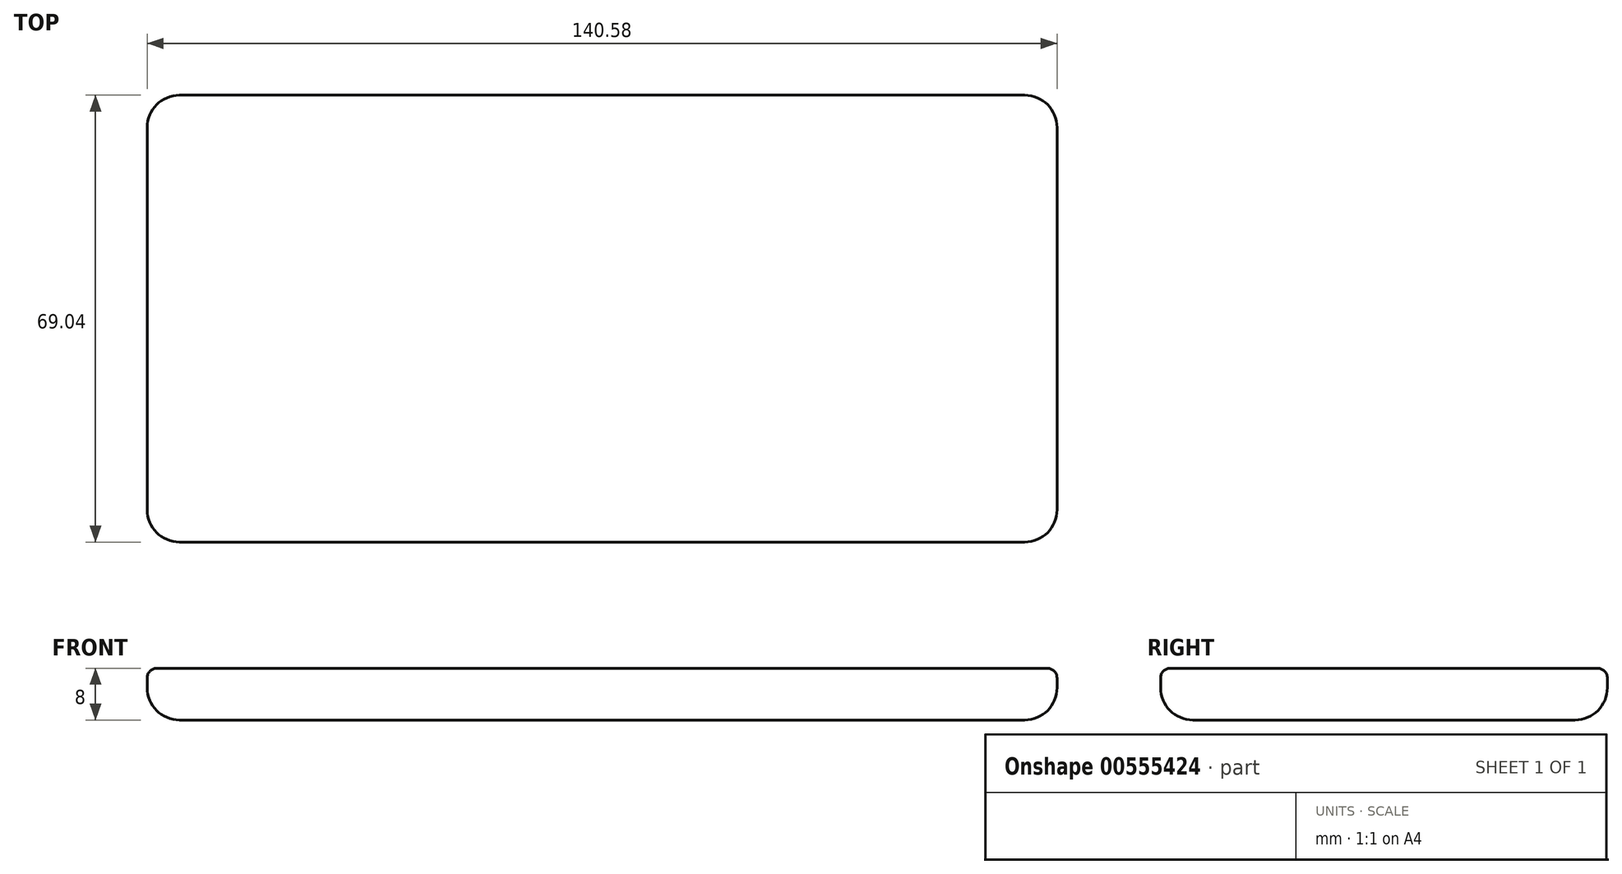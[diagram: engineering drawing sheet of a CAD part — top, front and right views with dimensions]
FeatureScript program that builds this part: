
annotation { "Feature Type Name" : "Feature", "Feature Type Description" : "" }
export const myFeature = defineFeature(function(context is Context, id is Id, definition is map)
    precondition{}
    {
        {
            var Q0;
            Q0=qCreatedBy(makeId("Top.planeOp"),FACE);
            var sketch = newSketch(context, id + "F0", { "sketchPlane" : qUnion([Q0])});
            skLineSegment(sketch, "E0.bottom", {"start": v(-65.3, 34.52) * mm, "end": v(65.3, 34.52) * mm});
            skLineSegment(sketch, "E0.top", {"start": v(-65.3, -34.52) * mm, "end": v(65.3, -34.52) * mm});
            skLineSegment(sketch, "E0.left", {"start": v(-70.3, 29.52) * mm, "end": v(-70.3, -29.52) * mm});
            skLineSegment(sketch, "E0.right", {"start": v(70.3, 29.52) * mm, "end": v(70.3, -29.52) * mm});
            skPoint(sketch, "E0.middle", {"position": v(0, 0) * mm});
            skPoint(sketch, "E1.visualSharp", {"position": v(-70.3, -34.52) * mm});
            skArc(sketch, "E1.filletArc", {"start": v(-70.3, -29.52) * mm, "mid": v(-68.83, -33.06) * mm, "end": v(-65.3, -34.52) * mm});
            skPoint(sketch, "E2.visualSharp", {"position": v(-70.3, 34.52) * mm});
            skArc(sketch, "E2.filletArc", {"start": v(-65.3, 34.52) * mm, "mid": v(-68.83, 33.06) * mm, "end": v(-70.3, 29.52) * mm});
            skPoint(sketch, "E3.visualSharp", {"position": v(70.3, 34.52) * mm});
            skArc(sketch, "E3.filletArc", {"start": v(70.3, 29.52) * mm, "mid": v(68.83, 33.06) * mm, "end": v(65.3, 34.52) * mm});
            skPoint(sketch, "E4.visualSharp", {"position": v(70.3, -34.52) * mm});
            skArc(sketch, "E4.filletArc", {"start": v(65.3, -34.52) * mm, "mid": v(68.83, -33.06) * mm, "end": v(70.3, -29.52) * mm});
            skSolve(sketch);
        }
        {
            var Q0;
            Q0=makeQuery(id+"F0.imprint","IMPRINT",FACE,{"disambiguationData":[TD([[makeQuery(id+"F0.imprint","IMPRINT",EDGE,{"derivedFrom":sQuery(id+"F0.wireOp",EDGE,"E0.bottom")}),-1.0]])]});
            extrude(context, id + "F1", {"entities" : qUnion([Q0]), "depth" : 8 * mm, "offsetDistance" : 25 * mm});
        }
        {
            var Q0;
            Q0=makeQuery(id+"F1.opExtrude","CAP_FACE",FACE,{"disambiguationData":[OSD([sQuery(id+"F0.wireOp",EDGE,"E0.bottom"),sQuery(id+"F0.wireOp",EDGE,"E0.top"),sQuery(id+"F0.wireOp",EDGE,"E0.left"),sQuery(id+"F0.wireOp",EDGE,"E0.right"),sQuery(id+"F0.wireOp",EDGE,"E1.filletArc"),sQuery(id+"F0.wireOp",EDGE,"E2.filletArc"),sQuery(id+"F0.wireOp",EDGE,"E3.filletArc"),sQuery(id+"F0.wireOp",EDGE,"E4.filletArc")])],"isStart":false});
            fillet(context, id + "F2", {"entities" : qUnion([Q0]), "radius" : 1.5 * mm, "tangentPropagation" : true, "allowEdgeOverflow" : false});
        }
        {
            var Q0;
            Q0=makeQuery(id+"F1.opExtrude","CAP_FACE",FACE,{"disambiguationData":[OSD([sQuery(id+"F0.wireOp",EDGE,"E0.bottom"),sQuery(id+"F0.wireOp",EDGE,"E0.top"),sQuery(id+"F0.wireOp",EDGE,"E0.left"),sQuery(id+"F0.wireOp",EDGE,"E0.right"),sQuery(id+"F0.wireOp",EDGE,"E1.filletArc"),sQuery(id+"F0.wireOp",EDGE,"E2.filletArc"),sQuery(id+"F0.wireOp",EDGE,"E3.filletArc"),sQuery(id+"F0.wireOp",EDGE,"E4.filletArc")])],"isStart":true});
            fillet(context, id + "F3", {"entities" : qUnion([Q0]), "radius" : 5 * mm, "tangentPropagation" : true, "allowEdgeOverflow" : false});
        }
    });
